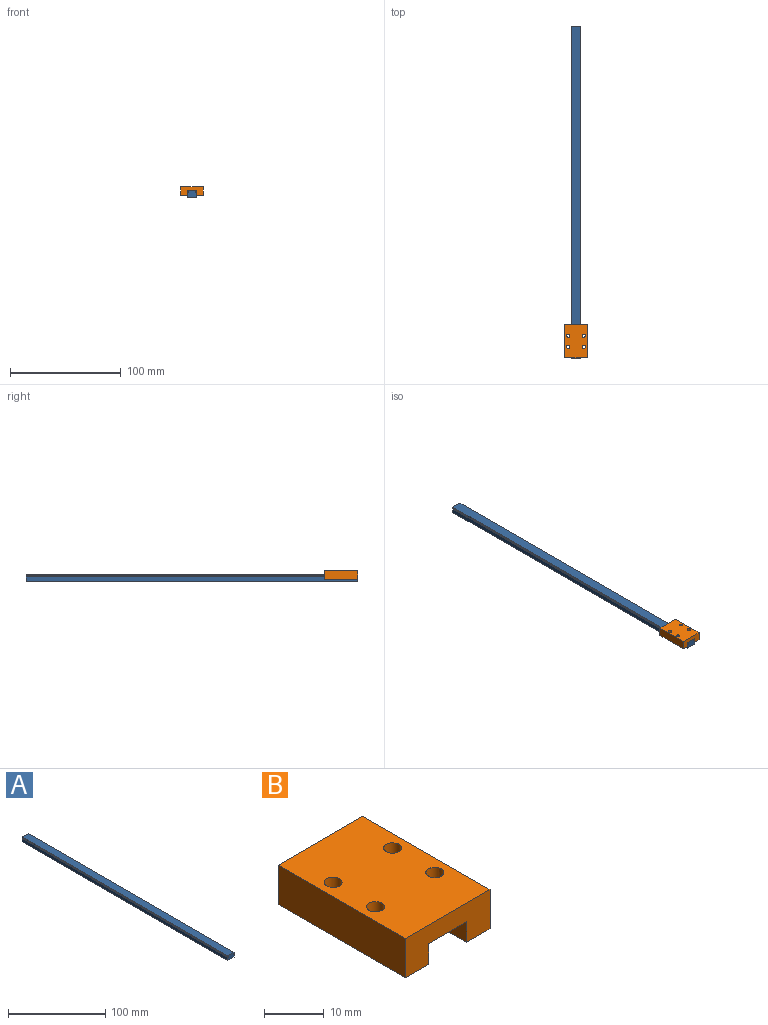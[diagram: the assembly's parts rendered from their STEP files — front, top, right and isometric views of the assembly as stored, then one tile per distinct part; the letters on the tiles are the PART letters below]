
ASSEMBLY  parts=2 mates=1
PART A: 14 faces, bbox 9x300x6 mm
  f0: plane 300x1mm, normal (-1,0,0), area 300mm2, adj f1,f11,f12,f13
  f1: plane 300x1mm, normal (0,0,-1), area 300mm2, adj f0,f2,f12,f13
  f2: plane 300x1mm, normal (-1,0,0), area 300mm2, adj f1,f3,f12,f13
  f3: plane 300x1mm, normal (0,0,1), area 300mm2, adj f2,f4,f12,f13
  f4: plane 300x4mm, normal (-1,0,0), area 1200mm2, adj f3,f5,f12,f13
  f5: plane 300x9mm, normal (0,0,-1), area 2700mm2, adj f4,f6,f12,f13
  f6: plane 300x4mm, normal (1,0,0), area 1200mm2, adj f5,f7,f12,f13
  f7: plane 300x1mm, normal (0,0,1), area 300mm2, adj f6,f8,f12,f13
  f8: plane 300x1mm, normal (1,0,0), area 300mm2, adj f7,f9,f12,f13
  f9: plane 300x1mm, normal (0,0,-1), area 300mm2, adj f8,f10,f12,f13
  f10: plane 300x1mm, normal (1,0,0), area 300mm2, adj f9,f11,f12,f13
  f11: plane 300x9mm, normal (0,0,1), area 2700mm2, adj f0,f10,f12,f13
  f12: plane 9x6mm, normal (0,-1,0), area 52mm2, adj f0,f1,f2,f3,f4,f5,f6,f7
  f13: plane 9x6mm, normal (0,1,0), area 52mm2, adj f0,f1,f2,f3,f4,f5,f6,f7
PART B: 14 faces, bbox 20x30x8 mm
  f0: plane 30x9mm, normal (0,0,-1), area 270mm2, adj f1,f7,f8,f9
  f1: plane 30x4.2mm, normal (-1,0,0), area 126mm2, adj f0,f2,f8,f9
  f2: plane 30x5.5mm, normal (0,0,-1), area 150.9mm2, adj f1,f3,f8,f9,f12,f13
  f3: plane 30x8mm, normal (1,0,0), area 240mm2, adj f2,f4,f8,f9
  f4: plane 30x20mm, normal (0,0,1), area 571.7mm2, adj f3,f5,f8,f9,f10,f11,f12,f13
  f5: plane 30x8mm, normal (-1,0,0), area 240mm2, adj f4,f6,f8,f9
  f6: plane 30x5.5mm, normal (0,0,-1), area 150.9mm2, adj f5,f7,f8,f9,f10,f11
  f7: plane 30x4.2mm, normal (1,0,0), area 126mm2, adj f0,f6,f8,f9
  f8: plane 20x8mm, normal (0,-1,0), area 122.2mm2, adj f0,f1,f2,f3,f4,f5,f6,f7
  f9: plane 20x8mm, normal (0,1,0), area 122.2mm2, adj f0,f1,f2,f3,f4,f5,f6,f7
  f10: cylinder r=1.5mm len=8mm, axis (0,0,1), area 75.4mm2, adj f4,f6
  f11: cylinder r=1.5mm len=8mm, axis (0,0,1), area 75.4mm2, adj f4,f6
  f12: cylinder r=1.5mm len=8mm, axis (0,0,1), area 75.4mm2, adj f2,f4
  f13: cylinder r=1.5mm len=8mm, axis (0,0,1), area 75.4mm2, adj f2,f4
PLACE A t=(-79.38,66.72,-58.08)mm fixed
PLACE B t=(-79.38,-203.28,-58.08)mm
MATE slider B.f8 <-> A.f12  axis (0,1,0) through (-83.88,-233.28,-55.08)mm
